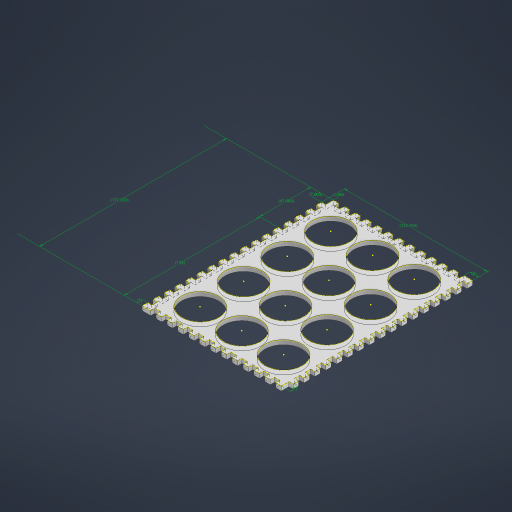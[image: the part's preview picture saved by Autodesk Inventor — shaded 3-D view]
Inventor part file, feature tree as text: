
AUTODESK INVENTOR PART (.ipt)
format: ipt  version: 2023 (Build 270158030, 158C)  size: 961,024 bytes
history: native  units: mm
features: direct_edit x4, sketch x3, extrude x2, delete_face x2, other x2, move_body x2, boolean_combine x1, projected_geometry x1
ambient origin geometry x8: Origin, YZ Plane, XZ Plane, XY Plane, X Axis, Y Axis, Z Axis, Center Point
bodies: Solid1 (feature_tree), Solid2 (feature_tree)
feature tree (17):
  extrude  "Extrusion1"  Depth=5.0mm
  extrude  "Extrusion2"  Depth=130.0mm
  direct_edit  "Direct Edit1"
  boolean_combine  "Combine1"
  direct_edit  "Direct Edit2"
  delete_face  "Delete Face1"
  direct_edit  "Direct Edit3"
  delete_face  "Delete Face2"
  direct_edit  "Direct Edit4"
  sketch  "Sketch4"  dims[d11=4.0mm d12=5.0mm d13=170.0mm d15=10.0mm d16=10.0mm d18=10.0mm d20=5.0mm d21=4.0mm d22=130.0mm d24=10.0mm d25=10.0mm d27=10.0mm d29=4.0mm d30=5.0mm d31=170.0mm d33=10.0mm d34=10.0mm d36=10.0mm d38=4.0mm d39=0.0mm d40=10.02mm d41=10.02mm d42=10.0mm d43=0.0mm d44=0.0mm d45=4.25mm d46=0.0mm d47=0.0mm d48=4.5mm d50=-0.3mm d51=132.004478mm d52=172.003386mm d53=7.003386mm d54=3.880396mm d55=47.003386mm d56=125.0mm d57=5.0mm d58=7.000109mm d59=8.0mm]
  sketch  "Sketch1"  dims[d0=4.0mm d1=0.0mm d2=5.0mm]
  sketch  "Sketch2"  dims[d3=4.0mm d4=130.0mm d6=10.0mm d7=10.0mm d9=10.0mm]
  projected_geometry  "Projected Loop2"
  other  "Scale1"
  move_body  "Move1"
  move_body  "Move2"
  other  "Size1"
